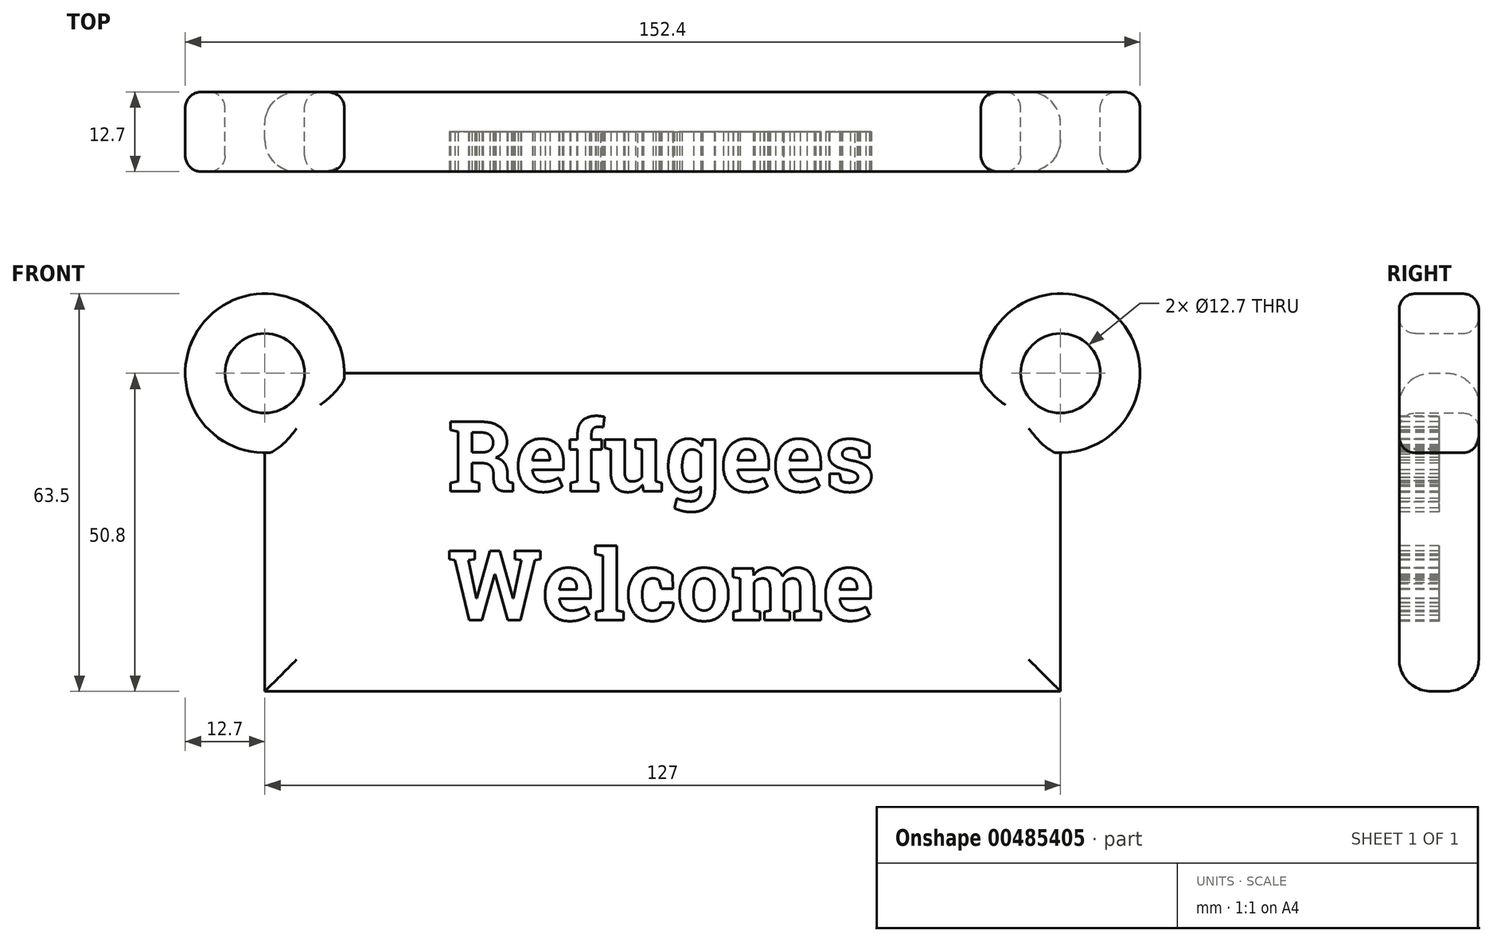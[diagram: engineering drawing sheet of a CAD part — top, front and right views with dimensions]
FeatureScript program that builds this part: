
annotation { "Feature Type Name" : "Feature", "Feature Type Description" : "" }
export const myFeature = defineFeature(function(context is Context, id is Id, definition is map)
    precondition{}
    {
        {
            var Q0;
            Q0=qCreatedBy(makeId("Front.planeOp"),FACE);
            var sketch = newSketch(context, id + "F0", { "sketchPlane" : qUnion([Q0])});
            skLineSegment(sketch, "E0.bottom", {"start": v(-127, 50.8) * mm, "end": v(0, 50.8) * mm});
            skLineSegment(sketch, "E0.top", {"start": v(-127, 0) * mm, "end": v(0, 0) * mm});
            skLineSegment(sketch, "E0.left", {"start": v(-127, 50.8) * mm, "end": v(-127, 0) * mm});
            skLineSegment(sketch, "E0.right", {"start": v(0, 50.8) * mm, "end": v(0, 0) * mm});
            skCircle(sketch, "E1", {"center": v(-127, 50.8) * mm, "radius": 6.35 * mm});
            skCircle(sketch, "E2", {"center": v(0, 50.8) * mm, "radius": 12.7 * mm});
            skCircle(sketch, "E3", {"center": v(0, 50.8) * mm, "radius": 6.35 * mm});
            skCircle(sketch, "E4", {"center": v(-127, 50.8) * mm, "radius": 12.7 * mm});
            skSolve(sketch);
        }
        {
            var Q0;
            Q0=qSketchRegion(id+"F0",true);
            extrude(context, id + "F1", {"entities" : qUnion([Q0]), "depth" : 12.7 * mm});
        }
        {
            var Q0;
            Q0=makeQuery(id+"F1.opExtrude","CAP_FACE",FACE,{"disambiguationData":[OSD([sQuery(id+"F0.wireOp",EDGE,"E0.bottom"),sQuery(id+"F0.wireOp",EDGE,"E0.top"),sQuery(id+"F0.wireOp",EDGE,"E0.left"),sQuery(id+"F0.wireOp",EDGE,"E0.right"),sQuery(id+"F0.wireOp",EDGE,"E1"),sQuery(id+"F0.wireOp",EDGE,"E2"),sQuery(id+"F0.wireOp",EDGE,"E3"),sQuery(id+"F0.wireOp",EDGE,"E4")])],"isStart":false});
            var sketch = newSketch(context, id + "F2", { "sketchPlane" : qUnion([Q0])});
            skText(sketch, "E5", { "text": "Refugees\nWelcome", "fontName": "RobotoSlab-Bold.ttf"});
            const initialGuessF2  = {"E5": [-0.09779, 0.03195, 1, 0, 0.01123]};
            skSetInitialGuess(sketch, initialGuessF2);
            skSolve(sketch);
        }
        {
            var Q0;
            Q0=qSketchRegion(id+"F2",true);
            extrude(context, id + "F3", {"entities" : qUnion([Q0]), "operationType" : NewBodyOperationType.REMOVE, "oppositeDirection" : true, "depth" : 6.35 * mm});
        }
        {
            var Q0;
            Q0=makeQuery(id+"F1.opExtrude","CAP_EDGE",EDGE,{"disambiguationData":[OSD([sQuery(id+"F0.wireOp",EDGE,"E1")])],"isStart":false});
            var Q1;
            Q1=makeQuery(id+"F1.opExtrude","CAP_EDGE",EDGE,{"disambiguationData":[OSD([sQuery(id+"F0.wireOp",EDGE,"E3")])],"isStart":false});
            var Q2;
            Q2=makeQuery(id+"F1.opExtrude","CAP_EDGE",EDGE,{"disambiguationData":[OSD([sQuery(id+"F0.wireOp",EDGE,"E1")])],"isStart":true});
            var Q3;
            Q3=makeQuery(id+"F1.opExtrude","CAP_EDGE",EDGE,{"disambiguationData":[OSD([sQuery(id+"F0.wireOp",EDGE,"E3")])],"isStart":true});
            var Q4;
            Q4=makeQuery(id+"F1.opExtrude","CAP_EDGE",EDGE,{"disambiguationData":[OSD([sQuery(id+"F0.wireOp",EDGE,"E4")])],"isStart":false});
            var Q5;
            Q5=makeQuery(id+"F1.opExtrude","CAP_EDGE",EDGE,{"disambiguationData":[OSD([sQuery(id+"F0.wireOp",EDGE,"E4")])],"isStart":true});
            var Q6;
            Q6=makeQuery(id+"F1.opExtrude","CAP_EDGE",EDGE,{"disambiguationData":[OSD([sQuery(id+"F0.wireOp",EDGE,"E2")])],"isStart":true});
            var Q7;
            Q7=makeQuery(id+"F1.opExtrude","CAP_EDGE",EDGE,{"disambiguationData":[OSD([sQuery(id+"F0.wireOp",EDGE,"E2")])],"isStart":false});
            fillet(context, id + "F4", {"entities" : qUnion([Q0, Q1, Q2, Q3, Q4, Q5, Q6, Q7]), "radius" : 2.54 * mm, "tangentPropagation" : true, "allowEdgeOverflow" : false});
        }
        {
            var Q0;
            Q0=makeQuery(id+"F1.opExtrude","CAP_EDGE",EDGE,{"disambiguationData":[OSD([sQuery(id+"F0.wireOp",EDGE,"E0.bottom")])],"isStart":false});
            var Q1;
            Q1=makeQuery(id+"F1.opExtrude","CAP_EDGE",EDGE,{"disambiguationData":[OSD([sQuery(id+"F0.wireOp",EDGE,"E0.bottom")])],"isStart":true});
            var Q2;
            Q2=makeQuery(id+"F1.opExtrude","CAP_EDGE",EDGE,{"disambiguationData":[OSD([sQuery(id+"F0.wireOp",EDGE,"E0.right")])],"isStart":false});
            var Q3;
            Q3=makeQuery(id+"F1.opExtrude","CAP_EDGE",EDGE,{"disambiguationData":[OSD([sQuery(id+"F0.wireOp",EDGE,"E0.right")])],"isStart":true});
            var Q4;
            Q4=makeQuery(id+"F1.opExtrude","CAP_EDGE",EDGE,{"disambiguationData":[OSD([sQuery(id+"F0.wireOp",EDGE,"E0.top")])],"isStart":false});
            var Q5;
            Q5=makeQuery(id+"F1.opExtrude","CAP_EDGE",EDGE,{"disambiguationData":[OSD([sQuery(id+"F0.wireOp",EDGE,"E0.left")])],"isStart":false});
            var Q6;
            Q6=makeQuery(id+"F1.opExtrude","CAP_EDGE",EDGE,{"disambiguationData":[OSD([sQuery(id+"F0.wireOp",EDGE,"E0.top")])],"isStart":true});
            var Q7;
            Q7=makeQuery(id+"F1.opExtrude","CAP_EDGE",EDGE,{"disambiguationData":[OSD([sQuery(id+"F0.wireOp",EDGE,"E0.left")])],"isStart":true});
            fillet(context, id + "F5", {"entities" : qUnion([Q0, Q1, Q2, Q3, Q4, Q5, Q6, Q7]), "radius" : 5.08 * mm, "tangentPropagation" : true, "allowEdgeOverflow" : false});
        }
    });
